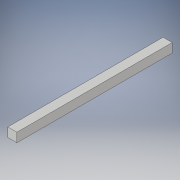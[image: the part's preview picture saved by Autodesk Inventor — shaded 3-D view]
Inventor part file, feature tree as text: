
AUTODESK INVENTOR PART (.ipt)
format: ipt  version: 2018 (Build 220112000, 112)  size: 92,672 bytes
history: native  units: in
note: dims shown in document units (in); Inventor stores cm internally (conversion verified against a paired STEP export)
features: extrude x1, sketch x1
ambient origin geometry x8: Origin, YZ Plane, XZ Plane, XY Plane, X Axis, Y Axis, Z Axis, Center Point
bodies: Solid1 (feature_tree)
feature tree (2):
  extrude  "Extrusion1"  Depth=17.0in
  sketch  "Sketch1"  dims[d0=1.0in d1=17.0in d2=1.0in d3=0.0in]
